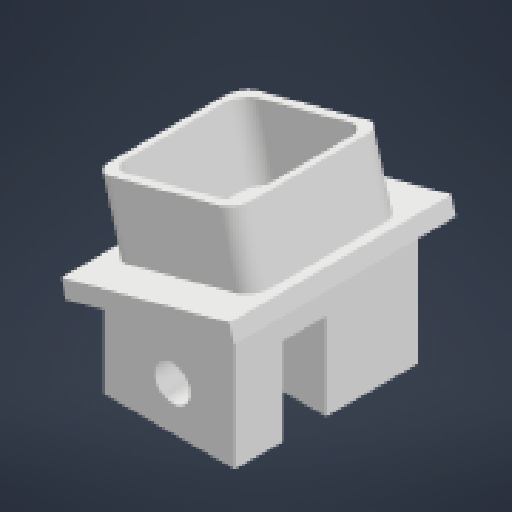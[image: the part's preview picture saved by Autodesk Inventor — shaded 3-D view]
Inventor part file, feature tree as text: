
AUTODESK INVENTOR PART (.ipt)
format: ipt  version: 2024 (Build 280153000, 153)  size: 196,096 bytes
history: native  units: mm
features: reference x11, extrude x5, sketch x5, other x4, fillet x1, projected_geometry x1
ambient origin geometry x8: Origin, YZ Plane, XZ Plane, XY Plane, X Axis, Y Axis, Z Axis, Center Point
bodies: Body1 (feature_tree)
feature tree (27):
  other  "Твердое тело1"
  extrude  "Выдавливание1"  Depth=10.0mm TaperAngle=0.0deg
  extrude  "Выдавливание2"  Depth=10.0mm TaperAngle=0.0deg
  extrude  "Выдавливание3"  Depth=1.745329mm
  extrude  "Выдавливание4"  Depth=10.0mm TaperAngle=0.0deg
  extrude  "Выдавливание5"  Depth=20.0mm
  fillet  "Сопряжение1"  Radius=2.0mm
  sketch  "Эскиз1"
  reference  "Ссылка1"
  reference  "Ссылка2"
  reference  "Ссылка3"
  reference  "Ссылка4"
  reference  "Ссылка5"
  reference  "Ссылка6"
  reference  "Ссылка7"
  reference  "Ссылка8"
  reference  "Ссылка16"
  reference  "Ссылка17"
  sketch  "Эскиз2"
  reference  "Ссылка18"
  sketch  "Эскиз3"
  sketch  "Эскиз4"
  projected_geometry  "Спроецированная петля1"
  sketch  "Эскиз5"
  parser-record x1  (decoder bookkeeping rows leaked as tree rows — omitted from the tree; the rows remain in map.json)
  other  "cum_holder_asembly.iam"
  other  "cum_holder_up:1"
note: 1 file-system path scrubbed to <path> (originals preserved in map.json)
